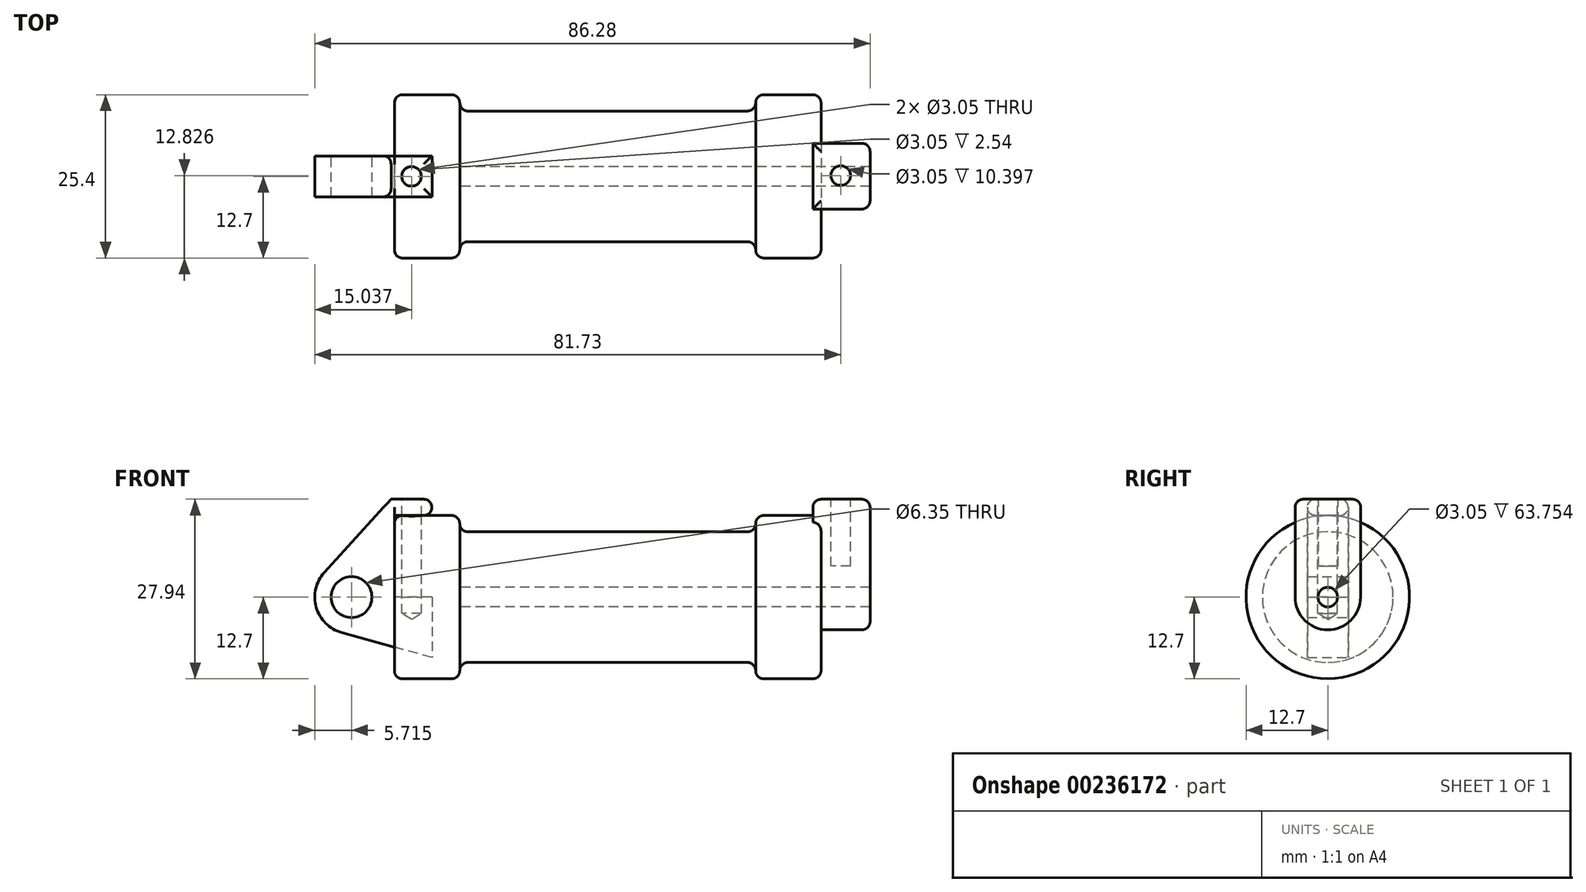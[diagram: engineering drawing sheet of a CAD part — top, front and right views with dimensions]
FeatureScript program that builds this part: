
annotation { "Feature Type Name" : "Feature", "Feature Type Description" : "" }
export const myFeature = defineFeature(function(context is Context, id is Id, definition is map)
    precondition{}
    {
        {
            var Q0;
            Q0=qCreatedBy(makeId("Front.planeOp"),FACE);
            var sketch = newSketch(context, id + "F0", { "sketchPlane" : qUnion([Q0])});
            skLineSegment(sketch, "E0", {"start": v(0, 0) * mm, "end": v(0, 12.7) * mm});
            skLineSegment(sketch, "E1", {"start": v(0, 12.7) * mm, "end": v(10.16, 12.7) * mm});
            skLineSegment(sketch, "E2", {"start": v(10.16, 12.7) * mm, "end": v(10.16, 10.16) * mm});
            skLineSegment(sketch, "E3", {"start": v(10.16, 10.16) * mm, "end": v(56.13, 10.16) * mm});
            skLineSegment(sketch, "E4", {"start": v(56.13, 10.16) * mm, "end": v(56.13, 12.7) * mm});
            skLineSegment(sketch, "E5", {"start": v(56.13, 12.7) * mm, "end": v(66.3, 12.7) * mm});
            skLineSegment(sketch, "E6", {"start": v(66.3, 12.7) * mm, "end": v(66.3, 0) * mm});
            skLineSegment(sketch, "E7", {"start": v(66.3, 0) * mm, "end": v(0, 0) * mm});
            skLineSegment(sketch, "E8", {"start": v(5.84, 15.24) * mm, "end": v(-0.5, 15.24) * mm});
            skLineSegment(sketch, "E9", {"start": v(-0.5, 15.24) * mm, "end": v(-10.88, 3.85) * mm});
            skLineSegment(sketch, "E10", {"start": v(0, 0) * mm, "end": v(-6.65, 0) * mm});
            skCircle(sketch, "E11", {"center": v(-6.65, 0) * mm, "radius": 5.72 * mm});
            skCircle(sketch, "E12", {"center": v(-6.65, 0) * mm, "radius": 3.18 * mm});
            skLineSegment(sketch, "E13", {"start": v(5.84, 15.24) * mm, "end": v(5.84, -9.4) * mm});
            skLineSegment(sketch, "E14", {"start": v(5.84, -9.4) * mm, "end": v(-8.18, -5.5) * mm});
            skSolve(sketch);
        }
        {
            var Q0;
            {var subQ0=sQuery(id+"F0.wireOp",EDGE,"E2");Q0=makeQuery(id+"F0.imprint","IMPRINT",FACE,{"disambiguationData":[TD([[makeQuery(id+"F0.imprint","IMPRINT",EDGE,{"derivedFrom":subQ0}),-1.0]])]});}
            var Q1;
            {var subQ0=sQuery(id+"F0.wireOp",EDGE,"E0");Q1=makeQuery(id+"F0.imprint","IMPRINT",FACE,{"disambiguationData":[TD([[makeQuery(id+"F0.imprint","IMPRINT",EDGE,{"derivedFrom":subQ0}),-1.0]])]});}
            var Q2;
            Q2=sQuery(id+"F0.wireOp",EDGE,"E7");
            revolve(context, id + "F1", {"entities" : qUnion([Q0, Q1]), "axis" : qUnion([Q2]), "revolveType" : RevolveType.FULL});
        }
        {
            var Q0;
            {var subQ3=sQuery(id+"F0.wireOp",EDGE,"E0");Q0=makeQuery(id+"F0.imprint","IMPRINT",FACE,{"disambiguationData":[TD([[makeQuery(id+"F0.imprint","IMPRINT",EDGE,{"derivedFrom":subQ3}),1.0]])]});}
            var Q1;
            {var subQ4=sQuery(id+"F0.wireOp",EDGE,"E12");Q1=makeQuery(id+"F0.imprint","IMPRINT",FACE,{"disambiguationData":[TD([[makeQuery(id+"F0.imprint","IMPRINT",EDGE,{"derivedFrom":subQ4}),-1.0]])]});}
            var Q2;
            {var subQ0=sQuery(id+"F0.wireOp",EDGE,"E14");Q2=makeQuery(id+"F0.imprint","IMPRINT",FACE,{"disambiguationData":[TD([[makeQuery(id+"F0.imprint","IMPRINT",EDGE,{"derivedFrom":subQ0}),-1.0]])]});}
            extrude(context, id + "F2", {"entities" : qUnion([Q0, Q1, Q2]), "endBound" : BoundingType.SYMMETRIC, "depth" : 6.35 * mm});
        }
        {
            var Q0;
            Q0=makeQuery(id+"F1.opRevolve","SWEPT_FACE",FACE,{"disambiguationData":[OSD([sQuery(id+"F0.wireOp",EDGE,"E6")])]});
            var sketch = newSketch(context, id + "F3", { "sketchPlane" : qUnion([Q0])});
            skCircle(sketch, "E15", {"center": v(0, 0) * mm, "radius": 1.52 * mm});
            skCircle(sketch, "E16", {"center": v(0, 0) * mm, "radius": 5.08 * mm});
            skLineSegment(sketch, "E17", {"start": v(-5.08, 0) * mm, "end": v(-5.08, 15.22) * mm});
            skLineSegment(sketch, "E18", {"start": v(-5.08, 15.22) * mm, "end": v(0.03, 15.22) * mm});
            skLineSegment(sketch, "E19", {"start": v(0.03, 15.22) * mm, "end": v(5.13, 15.22) * mm});
            skLineSegment(sketch, "E20", {"start": v(5.13, 15.22) * mm, "end": v(5.08, -0.02) * mm});
            skSolve(sketch);
        }
        {
            var Q0;
            Q0=makeQuery(id+"F3.imprint","IMPRINT",FACE,{"disambiguationData":[TD([[makeQuery(id+"F3.imprint","IMPRINT",EDGE,{"derivedFrom":sQuery(id+"F3.wireOp",EDGE,"E15")}),-1.0]])]});
            var Q1;
            {var subQ0=sQuery(id+"F3.wireOp",EDGE,"E17");var subQ1=sQuery(id+"F3.wireOp",EDGE,"E16");var subQ2=makeQuery(id+"F3.imprint","INTERSECT",VERTEX,{"derivedFrom":[subQ1,subQ0]});Q1=makeQuery(id+"F3.imprint","IMPRINT",FACE,{"disambiguationData":[TD([[makeQuery(id+"F3.imprint","IMPRINT",EDGE,{"disambiguationData":[TD([[subQ2,1.0]])],"derivedFrom":subQ1}),-1.0]])]});}
            var Q2;
            {var subQ4=sQuery(id+"F3.wireOp",EDGE,"E18");Q2=makeQuery(id+"F3.imprint","IMPRINT",FACE,{"disambiguationData":[TD([[makeQuery(id+"F3.imprint","IMPRINT",EDGE,{"derivedFrom":subQ4}),-1.0]])]});}
            extrude(context, id + "F4", {"entities" : qUnion([Q0, Q1, Q2]), "operationType" : NewBodyOperationType.ADD, "depth" : 7.62 * mm, "hasSecondDirection" : true, "secondDirectionOppositeDirection" : true, "secondDirectionDepth" : 1.27 * mm});
        }
        {
            var Q0;
            Q0=makeQuery(id+"F4.boolean.opBoolean","SPLIT",FACE,{"disambiguationData":[TD([makeQuery(id+"F4.opExtrude","SWEPT_FACE",FACE,{"disambiguationData":[OSD([sQuery(id+"F3.wireOp",EDGE,"E15")])]})])],"derivedFrom":makeQuery(id+"F1.opRevolve","SWEPT_FACE",FACE,{"disambiguationData":[OSD([sQuery(id+"F0.wireOp",EDGE,"E6")])]})});
            var Q1;
            Q1=makeQuery(id+"F1.opRevolve","SWEPT_FACE",FACE,{"disambiguationData":[OSD([sQuery(id+"F0.wireOp",EDGE,"E2")])]});
            extrude(context, id + "F5", {"entities" : qUnion([Q0]), "operationType" : NewBodyOperationType.REMOVE, "endBound" : BoundingType.UP_TO_SURFACE, "oppositeDirection" : true, "endBoundEntityFace" : qUnion([Q1]), "depth" : 25.4 * mm});
        }
        {
            var Q0;
            Q0=makeQuery(id+"F2.opExtrude","SWEPT_FACE",FACE,{"disambiguationData":[OSD([sQuery(id+"F0.wireOp",EDGE,"E8")])]});
            var sketch = newSketch(context, id + "F6", { "sketchPlane" : qUnion([Q0])});
            skCircle(sketch, "E21", {"center": v(2.67, 0) * mm, "radius": 1.52 * mm});
            skPoint(sketch, "E21.centerSnap0", {"position": v(-0.5, 0) * mm});
            skPoint(sketch, "E21.centerSnap1", {"position": v(2.67, -3.18) * mm});
            skCircle(sketch, "E22", {"center": v(69.36, 0.13) * mm, "radius": 1.52 * mm});
            skSolve(sketch);
        }
        {
            var Q0;
            Q0=makeQuery(id+"F6.imprint","IMPRINT",FACE,{"disambiguationData":[TD([[makeQuery(id+"F6.imprint","IMPRINT",EDGE,{"derivedFrom":sQuery(id+"F6.wireOp",EDGE,"E21")}),1.0]])]});
            var Q1;
            Q1=makeQuery(id+"F6.imprint","IMPRINT",FACE,{"disambiguationData":[TD([[makeQuery(id+"F6.imprint","IMPRINT",EDGE,{"derivedFrom":sQuery(id+"F6.wireOp",EDGE,"E22")}),1.0]])]});
            extrude(context, id + "F7", {"entities" : qUnion([Q0, Q1]), "operationType" : NewBodyOperationType.REMOVE, "oppositeDirection" : true, "depth" : 10.4 * mm});
        }
        {
            var Q0;
            Q0=sQuery(id+"F6.wireOp",VERTEX,"E21.center");
            var Q1;
            Q1=makeQuery(id+"F1.opRevolve","SWEPT_BODY",BODY,{"disambiguationData":[OSD([sQuery(id+"F0.wireOp",EDGE,"E0"),sQuery(id+"F0.wireOp",EDGE,"E1"),sQuery(id+"F0.wireOp",EDGE,"E2"),sQuery(id+"F0.wireOp",EDGE,"E3"),sQuery(id+"F0.wireOp",EDGE,"E4"),sQuery(id+"F0.wireOp",EDGE,"E5"),sQuery(id+"F0.wireOp",EDGE,"E6"),sQuery(id+"F0.wireOp",EDGE,"E7")])]});
            var Q2;
            Q2=makeQuery(id+"F2.opExtrude","SWEPT_BODY",BODY,{"disambiguationData":[OSD([sQuery(id+"F0.wireOp",EDGE,"E0"),sQuery(id+"F0.wireOp",EDGE,"E1"),sQuery(id+"F0.wireOp",EDGE,"E7"),sQuery(id+"F0.wireOp",EDGE,"E8"),sQuery(id+"F0.wireOp",EDGE,"E9"),sQuery(id+"F0.wireOp",EDGE,"E11"),sQuery(id+"F0.wireOp",EDGE,"E12"),sQuery(id+"F0.wireOp",EDGE,"E13"),sQuery(id+"F0.wireOp",EDGE,"E14")])]});
            hole(context, id + "F8", {"style" : HoleStyle.SIMPLE, "endStyle" : HoleEndStyle.BLIND, "holeDiameter" : 3.05 * mm, "holeDepth" : 17.78 * mm, "locations" : qUnion([Q0]), "scope" : qUnion([Q1, Q2])});
        }
        {
            var Q0;
            Q0=makeQuery(id+"F2.opExtrude","SWEPT_EDGE",EDGE,{"disambiguationData":[OSD([sQuery(id+"F0.wireOp",EDGE,"E8"),sQuery(id+"F0.wireOp",EDGE,"E13")])]});
            var Q1;
            Q1=makeQuery(id+"F2.opExtrude","CAP_EDGE",EDGE,{"disambiguationData":[OSD([sQuery(id+"F0.wireOp",EDGE,"E8")])],"isStart":false});
            var Q2;
            Q2=makeQuery(id+"F2.opExtrude","CAP_EDGE",EDGE,{"disambiguationData":[OSD([sQuery(id+"F0.wireOp",EDGE,"E8")])],"isStart":true});
            var Q3;
            Q3=makeQuery(id+"F4.opExtrude","CAP_EDGE",EDGE,{"disambiguationData":[OSD([sQuery(id+"F3.wireOp",EDGE,"E18"),sQuery(id+"F3.wireOp",EDGE,"E19")])],"isStart":false});
            var Q4;
            Q4=makeQuery(id+"F4.opExtrude","SWEPT_EDGE",EDGE,{"disambiguationData":[OSD([sQuery(id+"F3.wireOp",EDGE,"E17"),sQuery(id+"F3.wireOp",EDGE,"E18")])]});
            var Q5;
            Q5=makeQuery(id+"F4.opExtrude","CAP_EDGE",EDGE,{"disambiguationData":[OSD([sQuery(id+"F3.wireOp",EDGE,"E18"),sQuery(id+"F3.wireOp",EDGE,"E19")])],"isStart":true});
            var Q6;
            Q6=makeQuery(id+"F4.opExtrude","SWEPT_EDGE",EDGE,{"disambiguationData":[OSD([sQuery(id+"F3.wireOp",EDGE,"E19"),sQuery(id+"F3.wireOp",EDGE,"E20")])]});
            var Q7;
            Q7=makeQuery(id+"F4.opExtrude","CAP_EDGE",EDGE,{"disambiguationData":[OSD([sQuery(id+"F3.wireOp",EDGE,"E17")])],"isStart":false});
            var Q8;
            Q8=makeQuery(id+"F4.opExtrude","CAP_EDGE",EDGE,{"disambiguationData":[OSD([sQuery(id+"F3.wireOp",EDGE,"E20")])],"isStart":false});
            var Q9;
            Q9=makeQuery(id+"F1.opRevolve","SWEPT_EDGE",EDGE,{"disambiguationData":[OSD([sQuery(id+"F0.wireOp",EDGE,"E1"),sQuery(id+"F0.wireOp",EDGE,"E2")])]});
            var Q10;
            Q10=makeQuery(id+"F1.opRevolve","SWEPT_EDGE",EDGE,{"disambiguationData":[OSD([sQuery(id+"F0.wireOp",EDGE,"E4"),sQuery(id+"F0.wireOp",EDGE,"E5")])]});
            var Q11;
            Q11=makeQuery(id+"F1.opRevolve","SWEPT_EDGE",EDGE,{"disambiguationData":[OSD([sQuery(id+"F0.wireOp",EDGE,"E0"),sQuery(id+"F0.wireOp",EDGE,"E1")])]});
            var Q12;
            Q12=makeQuery(id+"F1.opRevolve","SWEPT_EDGE",EDGE,{"disambiguationData":[OSD([sQuery(id+"F0.wireOp",EDGE,"E5"),sQuery(id+"F0.wireOp",EDGE,"E6")])]});
            var Q13;
            Q13=makeQuery(id+"F1.opRevolve","SWEPT_EDGE",EDGE,{"disambiguationData":[OSD([sQuery(id+"F0.wireOp",EDGE,"E2"),sQuery(id+"F0.wireOp",EDGE,"E3")])]});
            var Q14;
            Q14=makeQuery(id+"F1.opRevolve","SWEPT_EDGE",EDGE,{"disambiguationData":[OSD([sQuery(id+"F0.wireOp",EDGE,"E3"),sQuery(id+"F0.wireOp",EDGE,"E4")])]});
            var Q15;
            Q15=makeQuery(id+"F2.opExtrude","CAP_EDGE",EDGE,{"disambiguationData":[OSD([sQuery(id+"F0.wireOp",EDGE,"E1")])],"isStart":false});
            var Q16;
            Q16=makeQuery(id+"F2.opExtrude","SWEPT_EDGE",EDGE,{"disambiguationData":[OSD([sQuery(id+"F0.wireOp",EDGE,"E1"),sQuery(id+"F0.wireOp",EDGE,"E13")])]});
            var Q17;
            Q17=makeQuery(id+"F2.opExtrude","CAP_EDGE",EDGE,{"disambiguationData":[OSD([sQuery(id+"F0.wireOp",EDGE,"E1")])],"isStart":true});
            fillet(context, id + "F9", {"entities" : qUnion([Q0, Q1, Q2, Q3, Q4, Q5, Q6, Q7, Q8, Q9, Q10, Q11, Q12, Q13, Q14, Q15, Q16, Q17]), "radius" : 1.27 * mm, "tangentPropagation" : true, "allowEdgeOverflow" : false});
        }
    });
